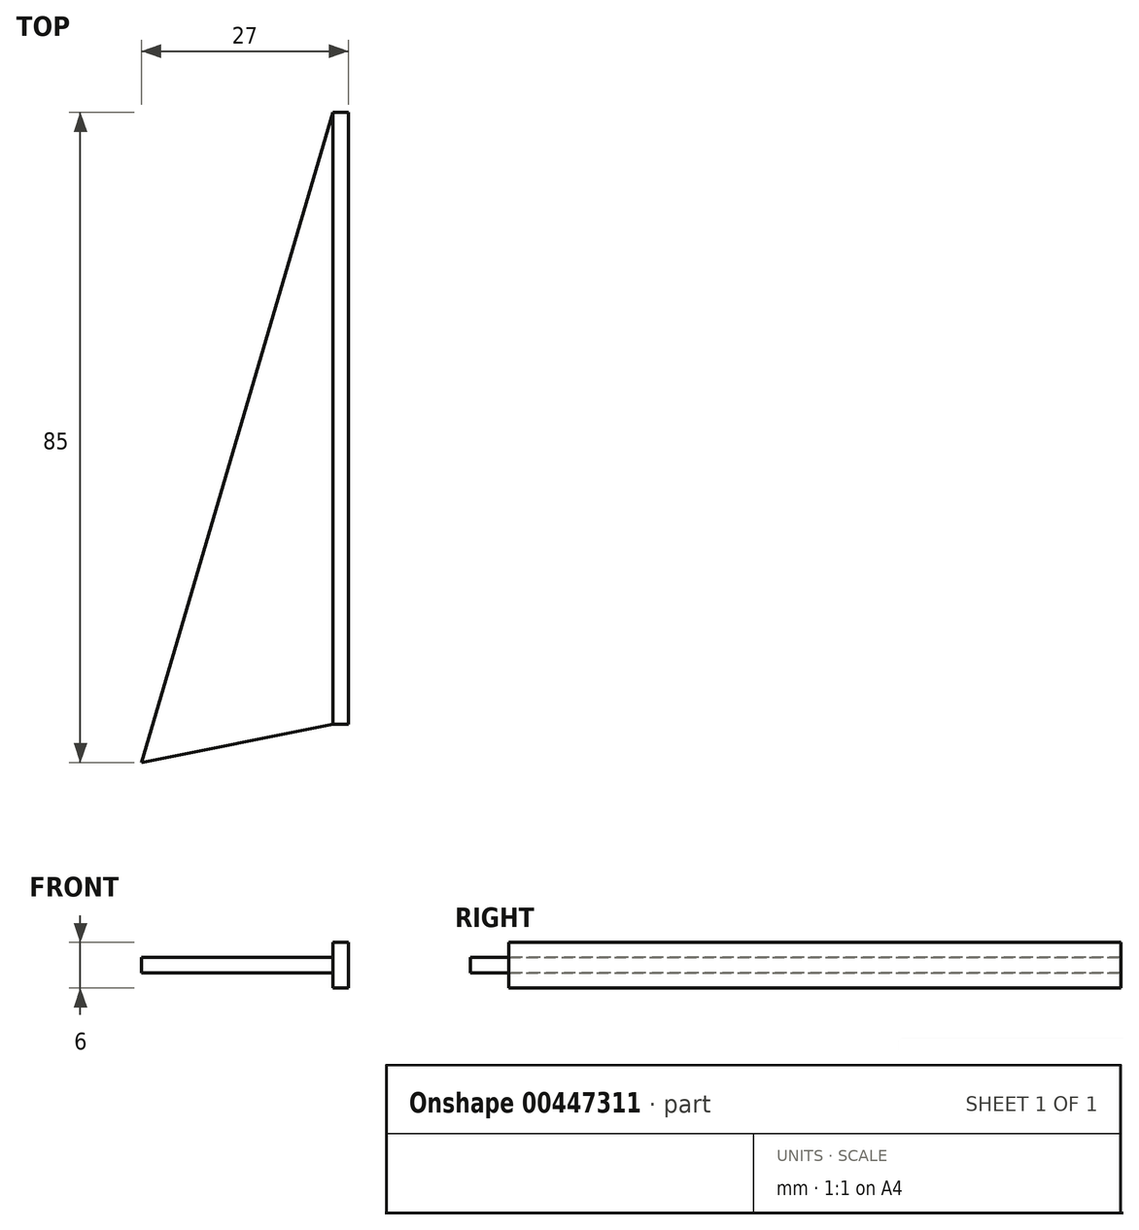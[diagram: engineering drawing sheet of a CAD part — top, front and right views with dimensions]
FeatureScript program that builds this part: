
annotation { "Feature Type Name" : "Feature", "Feature Type Description" : "" }
export const myFeature = defineFeature(function(context is Context, id is Id, definition is map)
    precondition{}
    {
        {
            var Q0;
            Q0=qCreatedBy(makeId("Top.planeOp"),FACE);
            var sketch = newSketch(context, id + "F0", { "sketchPlane" : qUnion([Q0])});
            skLineSegment(sketch, "E0", {"start": v(0, 0) * mm, "end": v(0, 80) * mm});
            skLineSegment(sketch, "E1", {"start": v(0, 80) * mm, "end": v(-25, -5) * mm});
            skLineSegment(sketch, "E2", {"start": v(-25, -5) * mm, "end": v(0, 0) * mm});
            skSolve(sketch);
        }
        {
            var Q0;
            Q0=makeQuery(id+"F0.imprint","IMPRINT",FACE,{"disambiguationData":[TD([[makeQuery(id+"F0.imprint","IMPRINT",EDGE,{"derivedFrom":sQuery(id+"F0.wireOp",EDGE,"E0")}),1.0]])]});
            extrude(context, id + "F1", {"entities" : qUnion([Q0]), "depth" : 2 * mm});
        }
        {
            var Q0;
            Q0=makeQuery(id+"F1.opExtrude","SWEPT_FACE",FACE,{"disambiguationData":[OSD([sQuery(id+"F0.wireOp",EDGE,"E0")])]});
            extrude(context, id + "F2", {"entities" : qUnion([Q0]), "operationType" : NewBodyOperationType.ADD, "depth" : 2 * mm});
        }
        {
            var Q0;
            {var subQ0=sQuery(id+"F0.wireOp",EDGE,"E0");Q0=makeQuery(id+"F2.boolean.opBoolean","MERGE",FACE,{"derivedFrom":[makeQuery(id+"F1.opExtrude","CAP_FACE",FACE,{"disambiguationData":[OSD([subQ0,sQuery(id+"F0.wireOp",EDGE,"E1"),sQuery(id+"F0.wireOp",EDGE,"E2")])],"isStart":false}),makeQuery(id+"F2.opExtrude","SWEPT_FACE",FACE,{"disambiguationData":[OSD([subQ0]),TDD([makeQuery(id+"F1.opExtrude","CAP_EDGE",EDGE,{"disambiguationData":[OSD([subQ0])],"isStart":false})])]})]});}
            var sketch = newSketch(context, id + "F3", { "sketchPlane" : qUnion([Q0])});
            skLineSegment(sketch, "E3.bottom", {"start": v(0, 0) * mm, "end": v(2, 0) * mm});
            skLineSegment(sketch, "E3.top", {"start": v(0, 80) * mm, "end": v(2, 80) * mm});
            skLineSegment(sketch, "E3.left", {"start": v(0, 0) * mm, "end": v(0, 80) * mm});
            skLineSegment(sketch, "E3.right", {"start": v(2, 0) * mm, "end": v(2, 80) * mm});
            skSolve(sketch);
        }
        {
            var Q0;
            Q0 = qSketchRegion(id + "F3", true);
            extrude(context, id + "F4", {"entities" : qUnion([Q0]), "operationType" : NewBodyOperationType.ADD, "depth" : 2 * mm});
        }
        {
            var Q0;
            Q0 = qSketchRegion(id + "F3", true);
            extrude(context, id + "F5", {"entities" : qUnion([Q0]), "operationType" : NewBodyOperationType.ADD, "oppositeDirection" : true, "depth" : 4 * mm});
        }
    });
